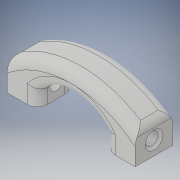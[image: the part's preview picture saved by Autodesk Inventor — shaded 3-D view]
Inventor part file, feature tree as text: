
AUTODESK INVENTOR PART (.ipt)
format: ipt  version: 2019 (Build 230136000, 136)  size: 190,464 bytes
history: native  units: mm
features: extrude x2, sketch x2, fillet x1, chamfer x1
ambient origin geometry x8: Origin, YZ Plane, XZ Plane, XY Plane, X Axis, Y Axis, Z Axis, Center Point
bodies: Solid1 (feature_tree)
feature tree (6):
  extrude  "Extrusion1"  Depth=10.0mm
  extrude  "Extrusion2"  Depth=9.0mm
  fillet  "Fillet1"  Radius=7.5mm
  chamfer  "Chamfer1"  Distance=2.5mm
  sketch  "Sketch1"  dims[d0=25.5mm d1=10.0mm]
  sketch  "Sketch2"  dims[d2=6.0mm d3=9.0mm d4=7.5mm d5=0.0mm d6=2.5mm d7=2.75mm d8=7.5mm d9=0.0mm d10=2.0mm d11=0.5mm d12=2.0mm d13=45.0deg d15=6.0mm]
